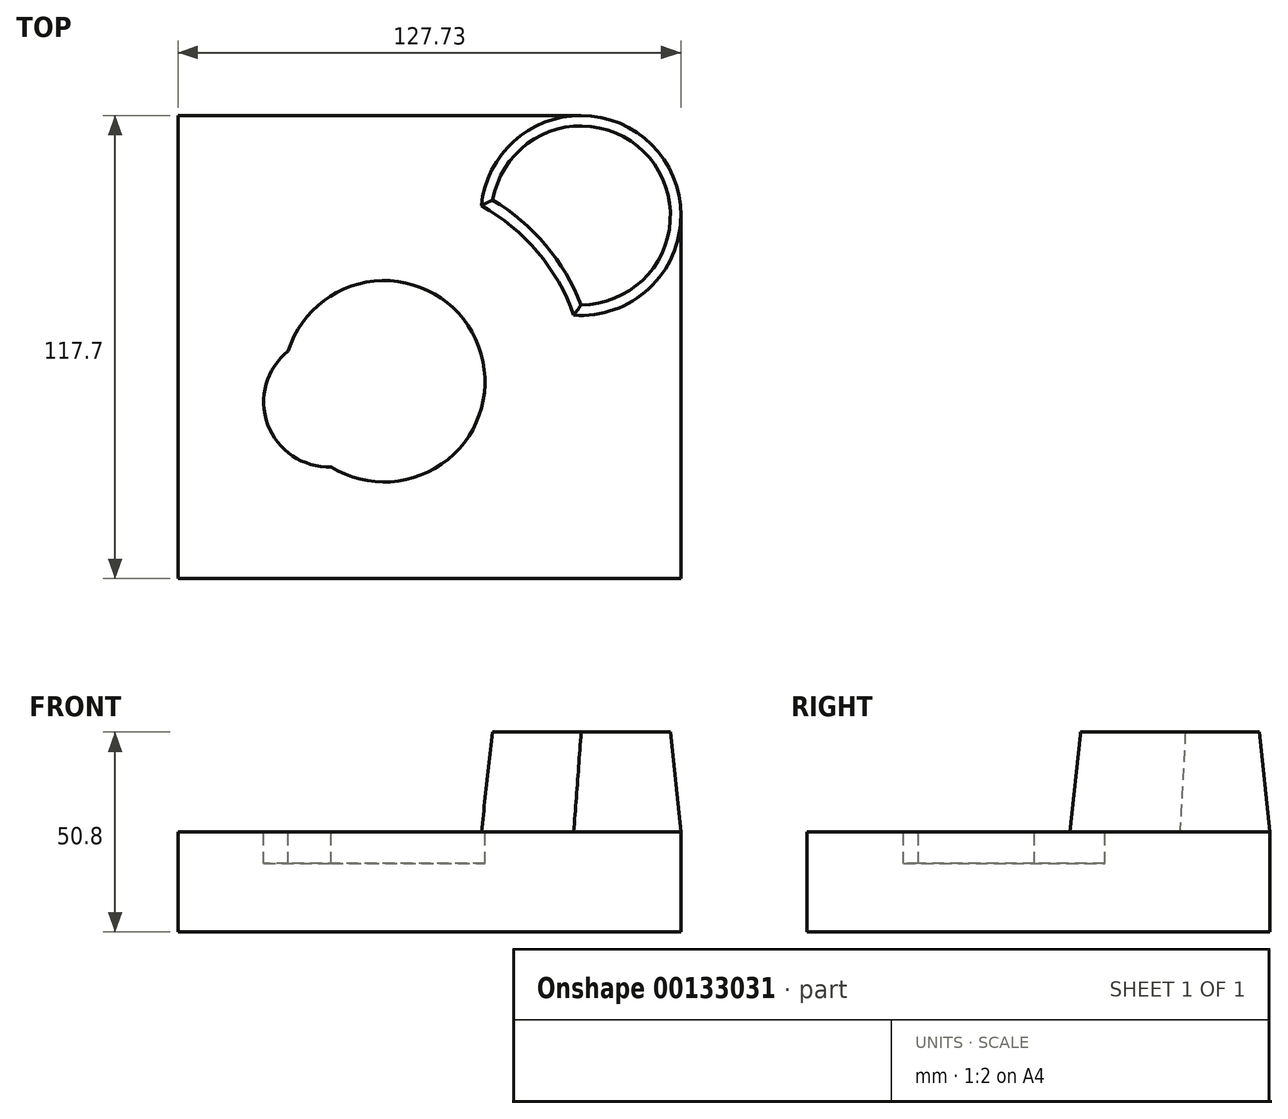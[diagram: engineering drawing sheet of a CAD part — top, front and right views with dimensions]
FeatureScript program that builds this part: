
annotation { "Feature Type Name" : "Feature", "Feature Type Description" : "" }
export const myFeature = defineFeature(function(context is Context, id is Id, definition is map)
    precondition{}
    {
        {
            var Q0;
            Q0=qCreatedBy(makeId("Top.planeOp"),FACE);
            var sketch = newSketch(context, id + "F0", { "sketchPlane" : qUnion([Q0])});
            skLineSegment(sketch, "E0.bottom", {"start": v(0, 0) * mm, "end": v(127.73, 0) * mm});
            skLineSegment(sketch, "E0.top", {"start": v(0, 117.7) * mm, "end": v(127.73, 117.7) * mm});
            skLineSegment(sketch, "E0.left", {"start": v(0, 0) * mm, "end": v(0, 117.7) * mm});
            skLineSegment(sketch, "E0.right", {"start": v(127.73, 0) * mm, "end": v(127.73, 117.7) * mm});
            skSolve(sketch);
        }
        {
            var Q0;
            Q0=makeQuery(id+"F0.imprint","IMPRINT",FACE,{"disambiguationData":[TD([[makeQuery(id+"F0.imprint","IMPRINT",EDGE,{"derivedFrom":sQuery(id+"F0.wireOp",EDGE,"E0.bottom")}),1.0]])]});
            extrude(context, id + "F1", {"entities" : qUnion([Q0]), "depth" : 25.4 * mm});
        }
        {
            var Q0;
            Q0=makeQuery(id+"F1.opExtrude","SWEPT_EDGE",EDGE,{"disambiguationData":[OSD([sQuery(id+"F0.wireOp",EDGE,"E0.top"),sQuery(id+"F0.wireOp",EDGE,"E0.right")])]});
            fillet(context, id + "F2", {"entities" : qUnion([Q0]), "radius" : 25.4 * mm, "tangentPropagation" : true, "allowEdgeOverflow" : false});
        }
        {
            var Q0;
            Q0=makeQuery(id+"F1.opExtrude","CAP_FACE",FACE,{"disambiguationData":[OSD([sQuery(id+"F0.wireOp",EDGE,"E0.bottom"),sQuery(id+"F0.wireOp",EDGE,"E0.top"),sQuery(id+"F0.wireOp",EDGE,"E0.left"),sQuery(id+"F0.wireOp",EDGE,"E0.right")])],"isStart":false});
            var sketch = newSketch(context, id + "F3", { "sketchPlane" : qUnion([Q0])});
            skArc(sketch, "E1", {"start": v(27.99, 57.87) * mm, "mid": v(22.78, 39.2) * mm, "end": v(38.87, 28.4) * mm});
            skArc(sketch, "E2", {"start": v(38.87, 28.4) * mm, "mid": v(76.38, 59) * mm, "end": v(27.99, 57.87) * mm});
            skSolve(sketch);
        }
        {
            var Q0;
            Q0=makeQuery(id+"F3.imprint","IMPRINT",FACE,{"disambiguationData":[TD([[makeQuery(id+"F3.imprint","IMPRINT",EDGE,{"derivedFrom":sQuery(id+"F3.wireOp",EDGE,"E1")}),1.0]])]});
            extrude(context, id + "F4", {"entities" : qUnion([Q0]), "operationType" : NewBodyOperationType.REMOVE, "oppositeDirection" : true, "depth" : 8 * mm});
        }
        {
            var Q0;
            Q0=makeQuery(id+"F1.opExtrude","CAP_FACE",FACE,{"disambiguationData":[OSD([sQuery(id+"F0.wireOp",EDGE,"E0.bottom"),sQuery(id+"F0.wireOp",EDGE,"E0.top"),sQuery(id+"F0.wireOp",EDGE,"E0.left"),sQuery(id+"F0.wireOp",EDGE,"E0.right")])],"isStart":false});
            var sketch = newSketch(context, id + "F5", { "sketchPlane" : qUnion([Q0])});
            skArc(sketch, "E3", {"start": v(100.5, 66.96) * mm, "mid": v(121.74, 108.68) * mm, "end": v(77.05, 94.75) * mm});
            skArc(sketch, "E4.0", {"start": v(100.5, 66.96) * mm, "mid": v(91.34, 83.02) * mm, "end": v(77.05, 94.75) * mm});
            skSolve(sketch);
        }
        {
            var Q0;
            {var subQ3=sQuery(id+"F5.wireOp",EDGE,"E4.0");Q0=makeQuery(id+"F5.imprint","IMPRINT",FACE,{"disambiguationData":[TD([[makeQuery(id+"F5.imprint","IMPRINT",EDGE,{"derivedFrom":subQ3}),-1.0]])]});}
            extrude(context, id + "F6", {"entities" : qUnion([Q0]), "operationType" : NewBodyOperationType.ADD, "depth" : 25.4 * mm, "hasDraft" : true, "draftAngle" : 6 * degree, "draftPullDirection" : true});
        }
    });
